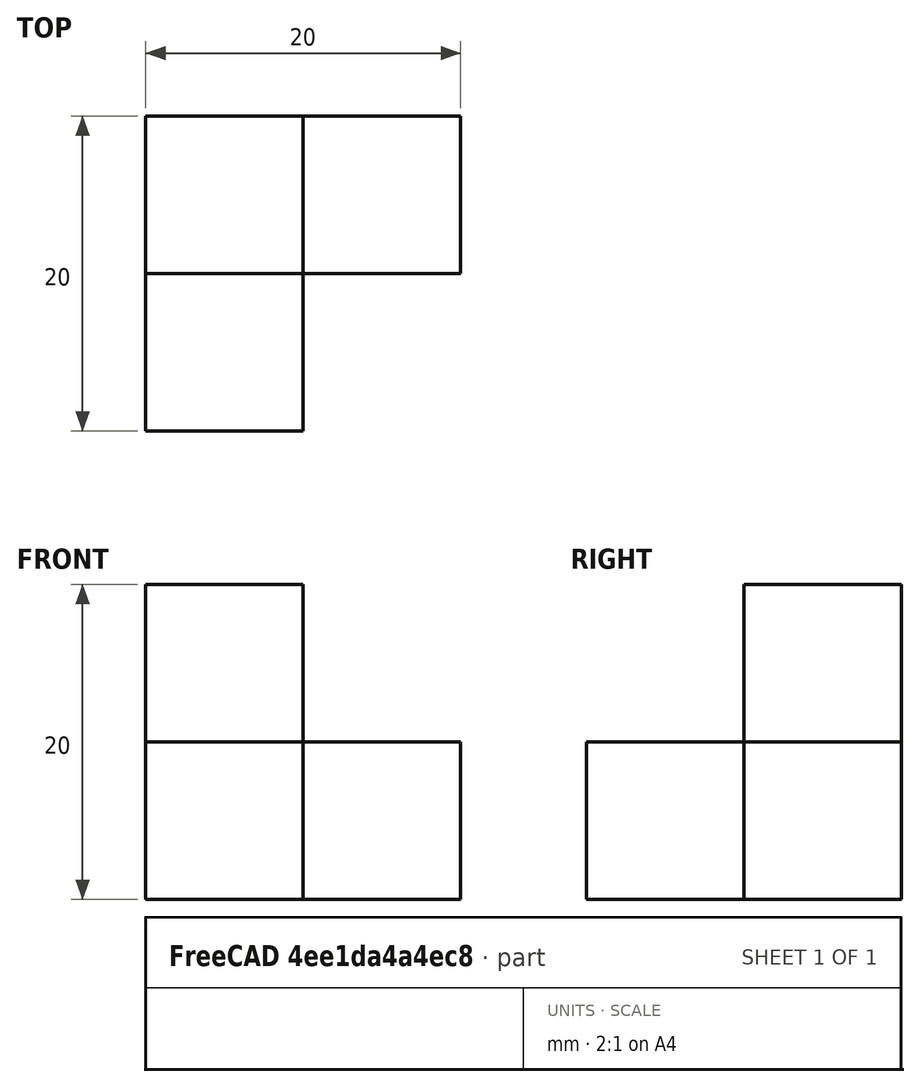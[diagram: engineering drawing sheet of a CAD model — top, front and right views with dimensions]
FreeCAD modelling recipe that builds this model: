
FCSTD DOCUMENT  (FreeCAD 0.21R33694 (Git))
Label: OJT1_T05R01_unions_qubert2
License: All rights reserved
LicenseURL: https://en.wikipedia.org/wiki/All_rights_reserved
objects: Part::Box×4, Part::MultiFuse×1, Part::Refine×1
note: 6 computed .brp shape members not serialized (recipe doc carries the construction recipe); baked Part::Feature solids carry a one-line shape summary decoded from their .brp

FEATURE [Part::Box] Box  label="Cub1_nivell1"
  AttacherType = Attacher::AttachEngine3D
  Height = 10
  Length = 10
  Placement = pos=(0,0,10) rot=(0,0,1;0rad)
  Width = 10
FEATURE [Part::Box] Box001  label="Cub2_nivell1"
  AttacherType = Attacher::AttachEngine3D
  Height = 10
  Length = 10
  Placement = pos=(10,0,0) rot=(0,0,1;0rad)
  Width = 10
FEATURE [Part::Box] Box002  label="Cub3_nivell1"
  AttacherType = Attacher::AttachEngine3D
  Height = 10
  Length = 10
  Placement = pos=(0,-10,0) rot=(0,0,1;0rad)
  Width = 10
FEATURE [Part::Box] Box003  label="Cub1_nivell002"
  AttacherType = Attacher::AttachEngine3D
  Height = 10
  Length = 10
  Width = 10
FEATURE [Part::MultiFuse] Fusion  label="qbert_2nivells"
  Shapes = -> [Box,Box001,Box002,Box003]
FEATURE [Part::Refine] Fusion001  label="qbert_2nivells001"
  Source = -> Fusion
